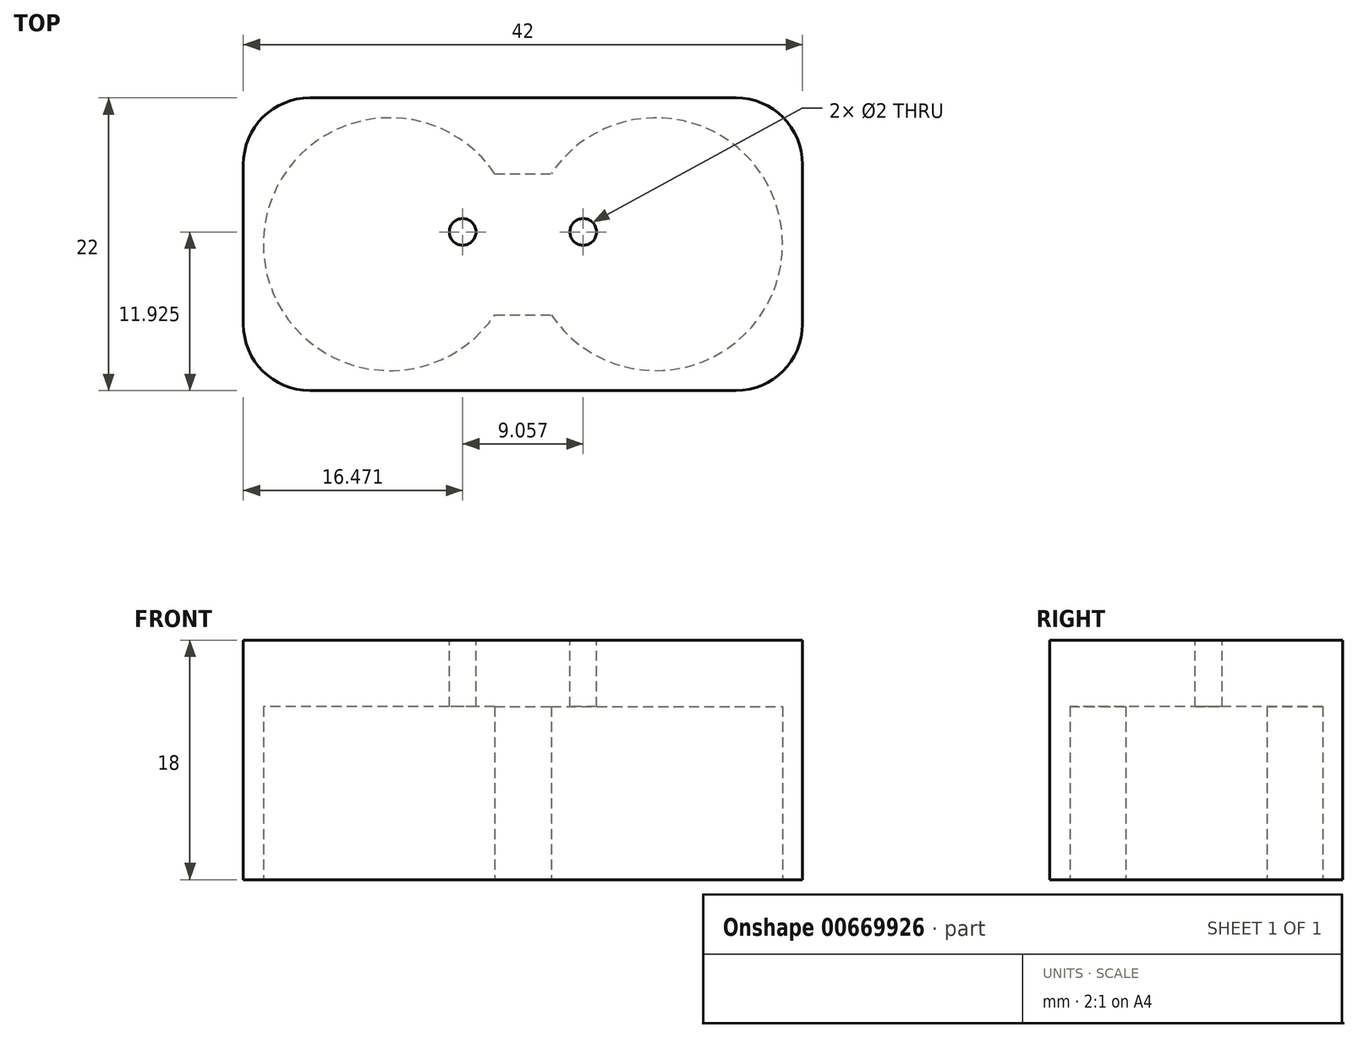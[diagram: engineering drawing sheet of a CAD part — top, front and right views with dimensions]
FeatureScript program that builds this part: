
annotation { "Feature Type Name" : "Feature", "Feature Type Description" : "" }
export const myFeature = defineFeature(function(context is Context, id is Id, definition is map)
    precondition{}
    {
        {
            var Q0;
            Q0=qCreatedBy(makeId("Top.planeOp"),FACE);
            var sketch = newSketch(context, id + "F0", { "sketchPlane" : qUnion([Q0])});
            skLineSegment(sketch, "E0.bottom", {"start": v(-21, 11) * mm, "end": v(21, 11) * mm});
            skLineSegment(sketch, "E0.top", {"start": v(-21, -11) * mm, "end": v(21, -11) * mm});
            skLineSegment(sketch, "E0.left", {"start": v(-21, 11) * mm, "end": v(-21, -11) * mm});
            skLineSegment(sketch, "E0.right", {"start": v(21, 11) * mm, "end": v(21, -11) * mm});
            skCircle(sketch, "E1", {"center": v(-10, 0) * mm, "radius": 9.5 * mm});
            skCircle(sketch, "E2", {"center": v(10, 0) * mm, "radius": 9.5 * mm});
            skLineSegment(sketch, "E3.bottom", {"start": v(-2.12, 5.3) * mm, "end": v(2.12, 5.3) * mm});
            skLineSegment(sketch, "E3.top", {"start": v(-2.12, -5.3) * mm, "end": v(2.12, -5.3) * mm});
            skLineSegment(sketch, "E3.left", {"start": v(-2.12, 5.3) * mm, "end": v(-2.12, -5.3) * mm});
            skLineSegment(sketch, "E3.right", {"start": v(2.12, 5.3) * mm, "end": v(2.12, -5.3) * mm});
            skSolve(sketch);
        }
        {
            var Q0;
            Q0 = qSketchRegion(id + "F0", true);
            extrude(context, id + "F1", {"entities" : qUnion([Q0]), "depth" : 13 * mm, "offsetDistance" : 25 * mm});
        }
        {
            var Q0;
            Q0=makeQuery(id+"F1.opExtrude","CAP_FACE",FACE,{"disambiguationData":[OSD([sQuery(id+"F0.wireOp",EDGE,"E0.bottom"),sQuery(id+"F0.wireOp",EDGE,"E0.top"),sQuery(id+"F0.wireOp",EDGE,"E0.left"),sQuery(id+"F0.wireOp",EDGE,"E0.right"),sQuery(id+"F0.wireOp",EDGE,"E1"),sQuery(id+"F0.wireOp",EDGE,"E2"),sQuery(id+"F0.wireOp",EDGE,"E3.bottom"),sQuery(id+"F0.wireOp",EDGE,"E3.top")])],"isStart":false});
            var sketch = newSketch(context, id + "F2", { "sketchPlane" : qUnion([Q0])});
            skLineSegment(sketch, "E4.bottom", {"start": v(-21, 11) * mm, "end": v(21, 11) * mm});
            skLineSegment(sketch, "E4.top", {"start": v(-21, -11) * mm, "end": v(21, -11) * mm});
            skLineSegment(sketch, "E4.left", {"start": v(-21, 11) * mm, "end": v(-21, -11) * mm});
            skLineSegment(sketch, "E4.right", {"start": v(21, 11) * mm, "end": v(21, -11) * mm});
            skSolve(sketch);
        }
        {
            var Q0;
            Q0 = qSketchRegion(id + "F2", true);
            extrude(context, id + "F3", {"entities" : qUnion([Q0]), "operationType" : NewBodyOperationType.ADD, "depth" : 5 * mm, "offsetDistance" : 25 * mm});
        }
        {
            var Q0;
            Q0=makeQuery(id+"F3.opExtrude","CAP_FACE",FACE,{"disambiguationData":[OSD([sQuery(id+"F2.wireOp",EDGE,"E4.bottom"),sQuery(id+"F2.wireOp",EDGE,"E4.top"),sQuery(id+"F2.wireOp",EDGE,"E4.left"),sQuery(id+"F2.wireOp",EDGE,"E4.right")])],"isStart":false});
            var sketch = newSketch(context, id + "F4", { "sketchPlane" : qUnion([Q0])});
            skCircle(sketch, "E5", {"center": v(-4.53, 0.92) * mm, "radius": 1 * mm});
            skCircle(sketch, "E6", {"center": v(4.53, 0.92) * mm, "radius": 1 * mm});
            skSolve(sketch);
        }
        {
            var Q0;
            Q0 = qSketchRegion(id + "F4", true);
            extrude(context, id + "F5", {"entities" : qUnion([Q0]), "operationType" : NewBodyOperationType.REMOVE, "oppositeDirection" : true, "depth" : 6 * mm, "offsetDistance" : 25 * mm});
        }
        {
            var Q0;
            Q0=makeQuery(id+"F3.boolean.opBoolean","MERGE",EDGE,{"derivedFrom":[makeQuery(id+"F1.opExtrude","SWEPT_EDGE",EDGE,{"disambiguationData":[OSD([sQuery(id+"F0.wireOp",EDGE,"E0.top"),sQuery(id+"F0.wireOp",EDGE,"E0.left")])]}),makeQuery(id+"F3.opExtrude","SWEPT_EDGE",EDGE,{"disambiguationData":[OSD([sQuery(id+"F2.wireOp",EDGE,"E4.top"),sQuery(id+"F2.wireOp",EDGE,"E4.left")])]})]});
            var Q1;
            Q1=makeQuery(id+"F3.boolean.opBoolean","MERGE",EDGE,{"derivedFrom":[makeQuery(id+"F1.opExtrude","SWEPT_EDGE",EDGE,{"disambiguationData":[OSD([sQuery(id+"F0.wireOp",EDGE,"E0.top"),sQuery(id+"F0.wireOp",EDGE,"E0.right")])]}),makeQuery(id+"F3.opExtrude","SWEPT_EDGE",EDGE,{"disambiguationData":[OSD([sQuery(id+"F2.wireOp",EDGE,"E4.top"),sQuery(id+"F2.wireOp",EDGE,"E4.right")])]})]});
            var Q2;
            Q2=makeQuery(id+"F3.boolean.opBoolean","MERGE",EDGE,{"derivedFrom":[makeQuery(id+"F1.opExtrude","SWEPT_EDGE",EDGE,{"disambiguationData":[OSD([sQuery(id+"F0.wireOp",EDGE,"E0.bottom"),sQuery(id+"F0.wireOp",EDGE,"E0.left")])]}),makeQuery(id+"F3.opExtrude","SWEPT_EDGE",EDGE,{"disambiguationData":[OSD([sQuery(id+"F2.wireOp",EDGE,"E4.bottom"),sQuery(id+"F2.wireOp",EDGE,"E4.left")])]})]});
            var Q3;
            Q3=makeQuery(id+"F3.boolean.opBoolean","MERGE",EDGE,{"derivedFrom":[makeQuery(id+"F1.opExtrude","SWEPT_EDGE",EDGE,{"disambiguationData":[OSD([sQuery(id+"F0.wireOp",EDGE,"E0.bottom"),sQuery(id+"F0.wireOp",EDGE,"E0.right")])]}),makeQuery(id+"F3.opExtrude","SWEPT_EDGE",EDGE,{"disambiguationData":[OSD([sQuery(id+"F2.wireOp",EDGE,"E4.bottom"),sQuery(id+"F2.wireOp",EDGE,"E4.right")])]})]});
            fillet(context, id + "F6", {"entities" : qUnion([Q0, Q1, Q2, Q3]), "radius" : 5 * mm, "tangentPropagation" : true, "allowEdgeOverflow" : false});
        }
    });
